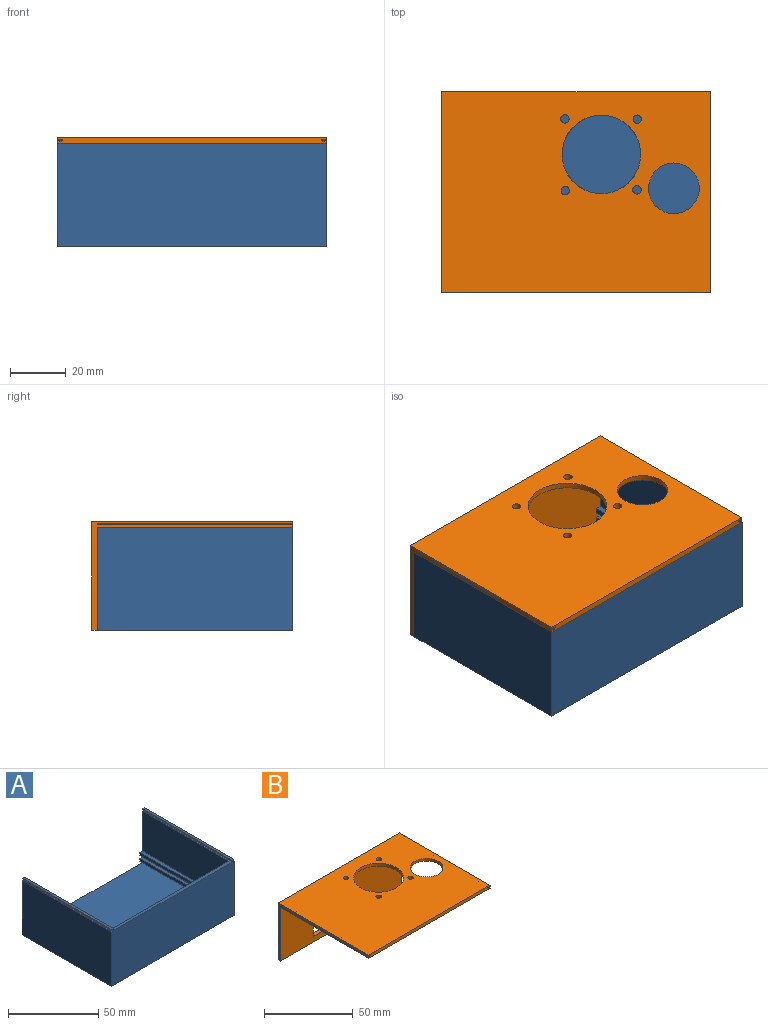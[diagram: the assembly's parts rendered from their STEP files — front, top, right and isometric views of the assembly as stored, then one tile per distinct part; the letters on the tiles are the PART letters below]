
ASSEMBLY  parts=2 mates=1
PART A: 42 faces, bbox 96.5x70x38.5 mm
  f0: plane 70x0.75mm, normal (0,0,1), area 52.5mm2, adj f3,f25,f27,f35
  f1: plane 94x70mm, normal (0,0,1), area 290mm2, adj f2,f7,f25,f26,f27,f28,f41
  f2: plane 68x27mm, normal (1,0,0), area 1836mm2, adj f1,f24,f25,f26
  f3: plane 70x37mm, normal (-1,0,0), area 2590mm2, adj f0,f4,f25,f27
  f4: plane 96.5x70mm, normal (0,0,-1), area 6755mm2, adj f3,f5,f25,f27
  f5: plane 70x37mm, normal (1,0,0), area 2590mm2, adj f4,f6,f25,f27
  f6: plane 70x0.75mm, normal (0,0,1), area 52.5mm2, adj f5,f25,f27,f34
  f7: plane 68x27mm, normal (-1,0,0), area 1836mm2, adj f1,f8,f25,f26
  f8: plane 68x2mm, normal (0,0,1), area 136mm2, adj f7,f9,f25,f26
  f9: plane 68x2mm, normal (-1,0,0), area 136mm2, adj f8,f10,f25,f26
  f10: plane 68x2mm, normal (0,0,-1), area 136mm2, adj f9,f11,f25,f26
  f11: plane 68x2mm, normal (-1,0,0), area 136mm2, adj f10,f12,f25,f26
  f12: plane 68x2mm, normal (0,0,1), area 136mm2, adj f11,f13,f25,f26
  f13: plane 68x2mm, normal (-1,0,0), area 136mm2, adj f12,f14,f25,f26
  f14: plane 68x2mm, normal (0,0,-1), area 136mm2, adj f13,f15,f25,f26
  f15: plane 68x2mm, normal (-1,0,0), area 136mm2, adj f14,f16,f25,f26
  f16: plane 92.5x68mm, normal (0,0,1), area 6290mm2, adj f15,f17,f25,f26
  f17: plane 68x2mm, normal (1,0,0), area 136mm2, adj f16,f18,f25,f26
  f18: plane 68x2mm, normal (0,0,-1), area 136mm2, adj f17,f19,f25,f26
  f19: plane 68x2mm, normal (1,0,0), area 136mm2, adj f18,f20,f25,f26
  f20: plane 68x2mm, normal (0,0,1), area 136mm2, adj f19,f21,f25,f26
  f21: plane 68x2mm, normal (1,0,0), area 136mm2, adj f20,f22,f25,f26
  f22: plane 68x2mm, normal (0,0,-1), area 136mm2, adj f21,f23,f25,f26
  f23: plane 68x2mm, normal (1,0,0), area 136mm2, adj f22,f24,f25,f26
  f24: plane 68x2mm, normal (0,0,1), area 136mm2, adj f2,f23,f25,f26
  f25: plane 96.5x38.5mm, normal (0,1,0), area 351.5mm2, adj f0,f1,f2,f3,f4,f5,f6,f7
  f26: plane 92.5x35mm, normal (0,1,0), area 3221.5mm2, adj f1,f2,f7,f8,f9,f10,f11,f12
  f27: plane 96.5x38.5mm, normal (0,-1,0), area 3573mm2, adj f0,f1,f3,f4,f5,f6,f28,f29
  f28: plane 70x1mm, normal (-1,0,0), area 70mm2, adj f1,f25,f27,f29
  f29: plane 70x0.5mm, normal (0,0,-1), area 35mm2, adj f25,f27,f28,f30
  f30: plane 70x0.5mm, normal (-1,0,0), area 35mm2, adj f25,f27,f29,f31
  f31: plane 70x1.5mm, normal (0,0,1), area 105mm2, adj f25,f27,f30,f32
  f32: plane 70x0.5mm, normal (1,0,0), area 35mm2, adj f25,f27,f31,f33
  f33: plane 70x0.5mm, normal (0,0,-1), area 35mm2, adj f25,f27,f32,f34
  f34: plane 70x1mm, normal (1,0,0), area 70mm2, adj f6,f25,f27,f33
  f35: plane 70x1mm, normal (-1,0,0), area 70mm2, adj f0,f25,f27,f36
  f36: plane 70x0.5mm, normal (0,0,-1), area 35mm2, adj f25,f27,f35,f37
  f37: plane 70x0.5mm, normal (-1,0,0), area 35mm2, adj f25,f27,f36,f38
  f38: plane 70x1.5mm, normal (0,0,1), area 105mm2, adj f25,f27,f37,f39
  f39: plane 70x0.5mm, normal (1,0,0), area 35mm2, adj f25,f27,f38,f40
  f40: plane 70x0.5mm, normal (0,0,-1), area 35mm2, adj f25,f27,f39,f41
  f41: plane 70x1mm, normal (1,0,0), area 70mm2, adj f1,f25,f27,f40
PART B: 34 faces, bbox 96.5x72x39 mm
  f0: plane 70x0.75mm, normal (0,0,-1), area 52.5mm2, adj f2,f10,f11,f33
  f1: plane 94x70mm, normal (0,0,-1), area 5661.7mm2, adj f2,f11,f14,f15,f16,f17,f18,f19
  f2: plane 96.5x2mm, normal (0,-1,0), area 190.5mm2, adj f0,f1,f4,f5,f10,f13,f20,f21
  f3: plane 96.5x2mm, normal (0,0,-1), area 193mm2, adj f4,f10,f11,f12
  f4: plane 72x39mm, normal (1,0,0), area 218mm2, adj f2,f3,f5,f11,f12,f13
  f5: plane 96.5x72mm, normal (0,0,1), area 6035.7mm2, adj f2,f4,f10,f12,f14,f15,f16,f17
  f6: plane 11x2mm, normal (1,0,0), area 22mm2, adj f7,f9,f11,f12
  f7: plane 9x2mm, normal (0,0,-1), area 18mm2, adj f6,f8,f11,f12
  f8: plane 11x2mm, normal (-1,0,0), area 22mm2, adj f7,f9,f11,f12
  f9: plane 9x2mm, normal (0,0,1), area 18mm2, adj f6,f8,f11,f12
  f10: plane 72x39mm, normal (-1,0,0), area 218mm2, adj f0,f2,f3,f5,f11,f12
  f11: plane 96.5x38.5mm, normal (0,-1,0), area 3474mm2, adj f0,f1,f3,f4,f6,f7,f8,f9
  f12: plane 96.5x39mm, normal (0,1,0), area 3664.5mm2, adj f3,f4,f5,f6,f7,f8,f9,f10
  f13: plane 70x0.75mm, normal (0,0,-1), area 52.5mm2, adj f2,f4,f11,f20
  f14: cone r=9.09mm half-angle=3deg, axis (0,0,-1), area 115.1mm2, adj f1,f5
  f15: cylinder r=1.5mm len=3mm, axis (0,0,1), area 18.8mm2, adj f1,f5
  f16: cylinder r=1.5mm len=3mm, axis (0,0,1), area 18.8mm2, adj f1,f5
  f17: cylinder r=1.5mm len=3mm, axis (0,0,1), area 18.8mm2, adj f1,f5
  f18: cylinder r=1.5mm len=3mm, axis (0,0,1), area 18.8mm2, adj f1,f5
  f19: cylinder r=14.1mm len=28.19mm, axis (0,0,1), area 177.1mm2, adj f1,f5
  f20: plane 70x1mm, normal (-1,0,0), area 70mm2, adj f2,f11,f13,f21
  f21: plane 70x0.5mm, normal (0,0,1), area 35mm2, adj f2,f11,f20,f22
  f22: plane 70x0.5mm, normal (-1,0,0), area 35mm2, adj f2,f11,f21,f23
  f23: plane 70x1.5mm, normal (0,0,-1), area 105mm2, adj f2,f11,f22,f24
  f24: plane 70x0.5mm, normal (1,0,0), area 35mm2, adj f2,f11,f23,f25
  f25: plane 70x0.5mm, normal (0,0,1), area 35mm2, adj f2,f11,f24,f26
  f26: plane 70x1mm, normal (1,0,0), area 70mm2, adj f1,f2,f11,f25
  f27: plane 70x1mm, normal (-1,0,0), area 70mm2, adj f1,f2,f11,f28
  f28: plane 70x0.5mm, normal (0,0,1), area 35mm2, adj f2,f11,f27,f29
  f29: plane 70x0.5mm, normal (-1,0,0), area 35mm2, adj f2,f11,f28,f30
  f30: plane 70x1.5mm, normal (0,0,-1), area 105mm2, adj f2,f11,f29,f31
  f31: plane 70x0.5mm, normal (1,0,0), area 35mm2, adj f2,f11,f30,f32
  f32: plane 70x0.5mm, normal (0,0,1), area 35mm2, adj f2,f11,f31,f33
  f33: plane 70x1mm, normal (1,0,0), area 70mm2, adj f0,f2,f11,f32
PLACE A t=(-12.3,-29.5,0)mm
PLACE B t=(-15.24,6.5,60.88)mm
MATE planar B.f0 <-> A.f0  axis (0,0,1) through (-60.55,-65.5,45.82)mm
